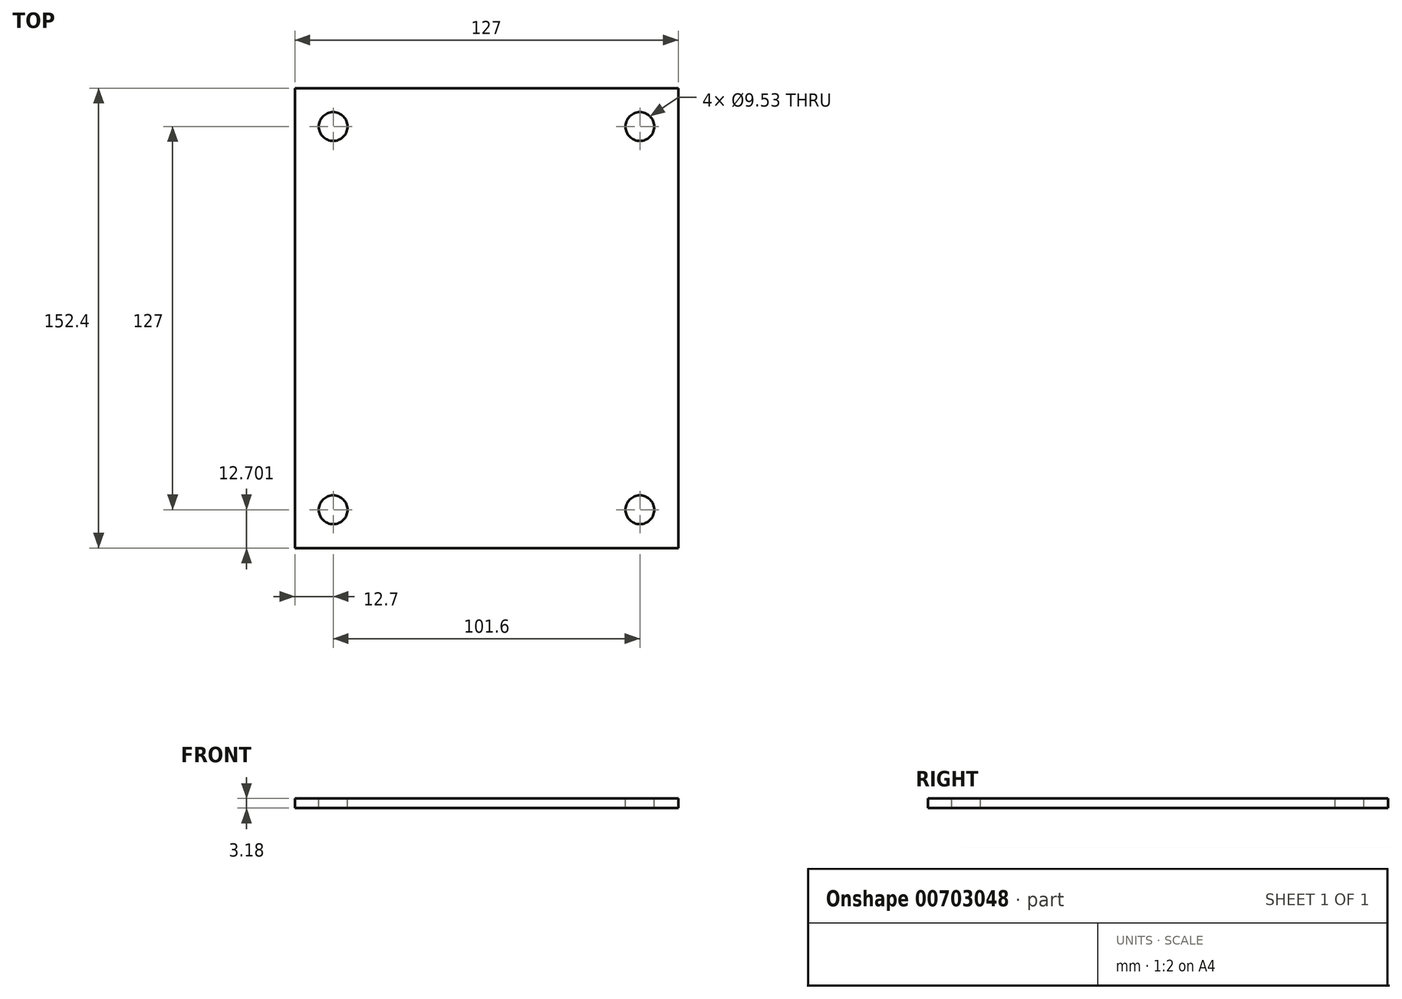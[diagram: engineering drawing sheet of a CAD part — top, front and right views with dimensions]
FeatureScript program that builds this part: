
annotation { "Feature Type Name" : "Feature", "Feature Type Description" : "" }
export const myFeature = defineFeature(function(context is Context, id is Id, definition is map)
    precondition{}
    {
        {
            var Q0;
            Q0=qCreatedBy(makeId("Top.planeOp"),FACE);
            var sketch = newSketch(context, id + "F0", { "sketchPlane" : qUnion([Q0])});
            skLineSegment(sketch, "E0.bottom", {"start": v(-63.5, 75.25) * mm, "end": v(63.5, 75.25) * mm});
            skLineSegment(sketch, "E0.top", {"start": v(-63.5, -77.15) * mm, "end": v(63.5, -77.15) * mm});
            skLineSegment(sketch, "E0.left", {"start": v(-63.5, 75.25) * mm, "end": v(-63.5, -77.15) * mm});
            skLineSegment(sketch, "E0.right", {"start": v(63.5, 75.25) * mm, "end": v(63.5, -77.15) * mm});
            skSolve(sketch);
        }
        {
            var Q0;
            Q0=makeQuery(id+"F0.imprint","IMPRINT",FACE,{"disambiguationData":[TD([[makeQuery(id+"F0.imprint","IMPRINT",EDGE,{"derivedFrom":sQuery(id+"F0.wireOp",EDGE,"E0.bottom")}),-1.0]])]});
            extrude(context, id + "F1", {"entities" : qUnion([Q0]), "depth" : 3.17 * mm, "offsetDistance" : 25.4 * mm});
        }
        {
            var Q0;
            Q0=makeQuery(id+"F1.opExtrude","CAP_FACE",FACE,{"disambiguationData":[OSD([sQuery(id+"F0.wireOp",EDGE,"E0.bottom"),sQuery(id+"F0.wireOp",EDGE,"E0.top"),sQuery(id+"F0.wireOp",EDGE,"E0.left"),sQuery(id+"F0.wireOp",EDGE,"E0.right")])],"isStart":false});
            var sketch = newSketch(context, id + "F2", { "sketchPlane" : qUnion([Q0])});
            skCircle(sketch, "E1", {"center": v(-50.8, 62.55) * mm, "radius": 4.76 * mm});
            skCircle(sketch, "E2", {"center": v(50.8, 62.55) * mm, "radius": 4.76 * mm});
            skCircle(sketch, "E3", {"center": v(-50.8, -64.45) * mm, "radius": 4.76 * mm});
            skCircle(sketch, "E4", {"center": v(50.8, -64.45) * mm, "radius": 4.76 * mm});
            skSolve(sketch);
        }
        {
            var Q0;
            Q0=makeQuery(id+"F2.imprint","IMPRINT",FACE,{"disambiguationData":[TD([[makeQuery(id+"F2.imprint","IMPRINT",EDGE,{"derivedFrom":sQuery(id+"F2.wireOp",EDGE,"E3")}),1.0]])]});
            var Q1;
            Q1=makeQuery(id+"F2.imprint","IMPRINT",FACE,{"disambiguationData":[TD([[makeQuery(id+"F2.imprint","IMPRINT",EDGE,{"derivedFrom":sQuery(id+"F2.wireOp",EDGE,"E4")}),1.0]])]});
            var Q2;
            Q2=makeQuery(id+"F2.imprint","IMPRINT",FACE,{"disambiguationData":[TD([[makeQuery(id+"F2.imprint","IMPRINT",EDGE,{"derivedFrom":sQuery(id+"F2.wireOp",EDGE,"E1")}),1.0]])]});
            var Q3;
            Q3=makeQuery(id+"F2.imprint","IMPRINT",FACE,{"disambiguationData":[TD([[makeQuery(id+"F2.imprint","IMPRINT",EDGE,{"derivedFrom":sQuery(id+"F2.wireOp",EDGE,"E2")}),1.0]])]});
            var Q4;
            Q4=sQuery(id+"F2.wireOp",EDGE,"E3");
            extrude(context, id + "F3", {"entities" : qUnion([Q0, Q1, Q2, Q3]), "operationType" : NewBodyOperationType.REMOVE, "surfaceEntities" : qUnion([Q4]), "oppositeDirection" : true, "depth" : 25.4 * mm, "offsetDistance" : 25.4 * mm});
        }
    });
